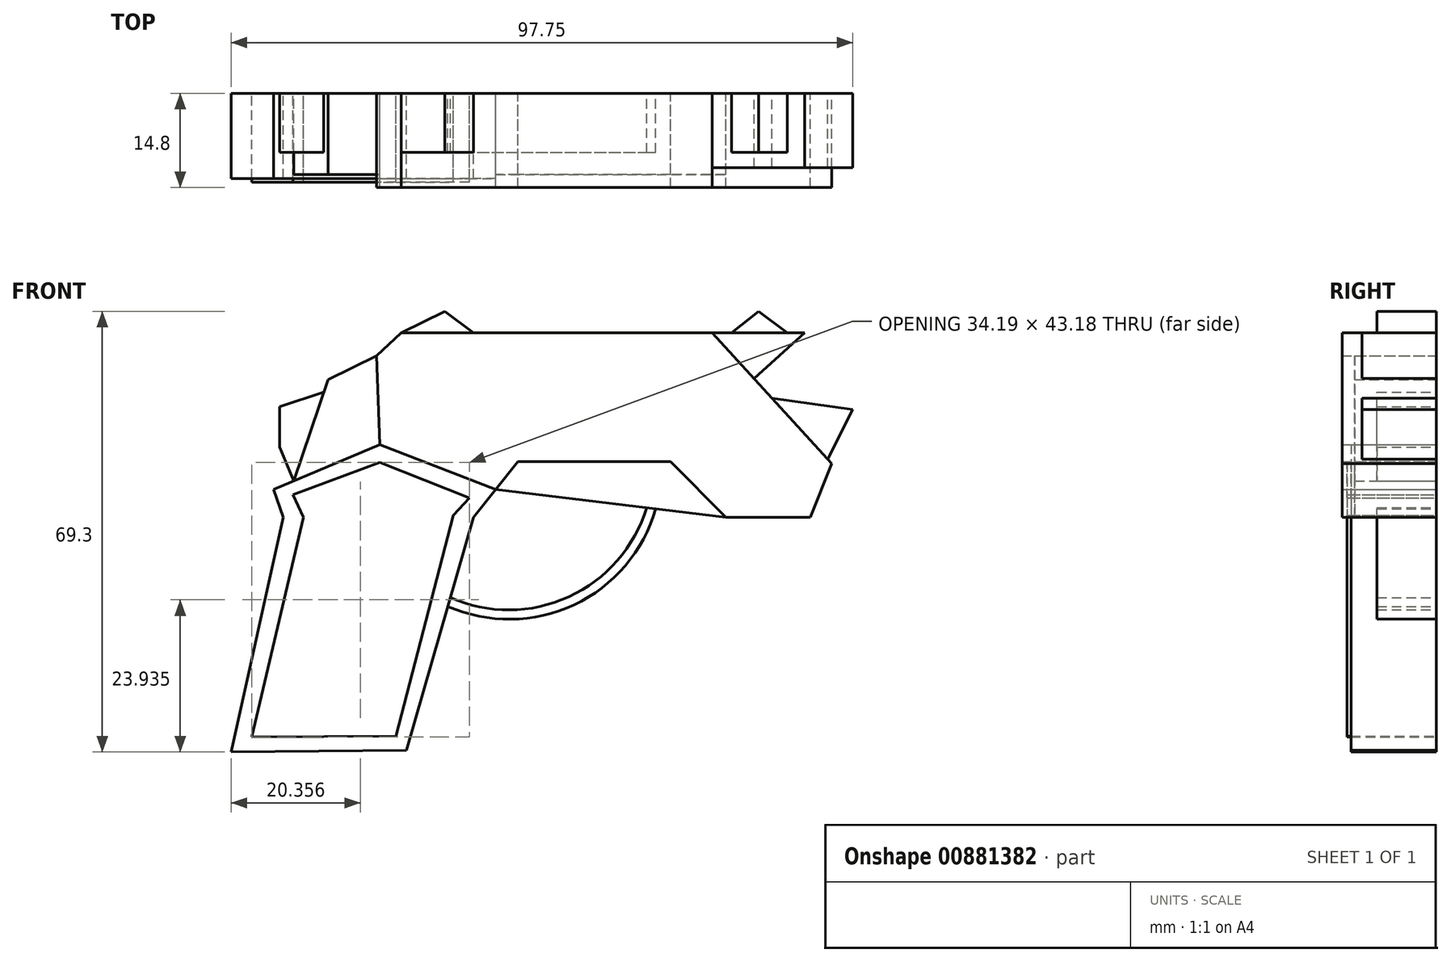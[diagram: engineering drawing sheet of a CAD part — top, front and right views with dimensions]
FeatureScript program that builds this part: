
annotation { "Feature Type Name" : "Feature", "Feature Type Description" : "" }
export const myFeature = defineFeature(function(context is Context, id is Id, definition is map)
    precondition{}
    {
        {
            var Q0;
            Q0=qCreatedBy(makeId("Front.planeOp"),FACE);
            var sketch = newSketch(context, id + "F0", { "sketchPlane" : qUnion([Q0])});
            skLineSegment(sketch, "E0", {"start": v(-19.98, -27.94) * mm, "end": v(-9.39, 8.68) * mm});
            skLineSegment(sketch, "E1", {"start": v(-9.39, 37.73) * mm, "end": v(-13.93, 41.06) * mm});
            skLineSegment(sketch, "E2", {"start": v(-39.34, 8.68) * mm, "end": v(-47.52, -28.24) * mm});
            skLineSegment(sketch, "E3", {"start": v(-47.52, -28.24) * mm, "end": v(-19.98, -27.94) * mm});
            skLineSegment(sketch, "E4", {"start": v(30.26, 8.68) * mm, "end": v(43.57, 8.68) * mm});
            skLineSegment(sketch, "E5", {"start": v(30.26, 8.68) * mm, "end": v(21.6, 17.45) * mm});
            skLineSegment(sketch, "E6", {"start": v(21.6, 17.45) * mm, "end": v(-2.43, 17.45) * mm});
            skLineSegment(sketch, "E7", {"start": v(46.9, 17.15) * mm, "end": v(28.14, 37.73) * mm});
            skLineSegment(sketch, "E8", {"start": v(-2.43, 17.45) * mm, "end": v(-9.39, 8.68) * mm});
            skLineSegment(sketch, "E9", {"start": v(42.66, 37.73) * mm, "end": v(28.14, 37.73) * mm});
            skLineSegment(sketch, "E10", {"start": v(50.23, 25.62) * mm, "end": v(37.52, 27.44) * mm});
            skLineSegment(sketch, "E11", {"start": v(-5.9, 13.06) * mm, "end": v(30.26, 8.68) * mm});
            skArc(sketch, "E12", {"start": v(-13.04, -3.94) * mm, "mid": v(5.57, -3.83) * mm, "end": v(17.81, 10.19) * mm});
            skLineSegment(sketch, "E13", {"start": v(-7.65, 10.87) * mm, "end": v(-12.14, -4.32) * mm});
            skLineSegment(sketch, "E14", {"start": v(0.63, 6.64) * mm, "end": v(-1.72, 0) * mm});
            skLineSegment(sketch, "E15", {"start": v(0, 7.28) * mm, "end": v(-2.68, 0) * mm});
            skLineSegment(sketch, "E16", {"start": v(-2.68, 0) * mm, "end": v(-0.76, -5.67) * mm});
            skLineSegment(sketch, "E17", {"start": v(0, 7.28) * mm, "end": v(5.01, 11.74) * mm});
            skLineSegment(sketch, "E18", {"start": v(0.63, 6.64) * mm, "end": v(2.5, 9.5) * mm});
            skLineSegment(sketch, "E19", {"start": v(-1.72, 0) * mm, "end": v(-1.72, -2.83) * mm});
            skArc(sketch, "E20", {"start": v(-13.44, -5.33) * mm, "mid": v(6.4, -5.08) * mm, "end": v(19.25, 10.01) * mm});
            skLineSegment(sketch, "E21", {"start": v(41.03, 36.24) * mm, "end": v(46.3, 36.24) * mm});
            skLineSegment(sketch, "E22", {"start": v(46.3, 36.24) * mm, "end": v(46.3, 26.7) * mm});
            skLineSegment(sketch, "E23", {"start": v(46.3, 26.7) * mm, "end": v(42.66, 26.7) * mm});
            skLineSegment(sketch, "E24", {"start": v(48.73, 34.52) * mm, "end": v(48.73, 28.62) * mm});
            skLineSegment(sketch, "E25", {"start": v(48.73, 28.62) * mm, "end": v(46.3, 26.7) * mm});
            skLineSegment(sketch, "E26", {"start": v(48.73, 34.52) * mm, "end": v(46.3, 36.24) * mm});
            skLineSegment(sketch, "E27", {"start": v(46.9, 17.15) * mm, "end": v(43.57, 8.68) * mm});
            skLineSegment(sketch, "E28", {"start": v(50.23, 25.62) * mm, "end": v(46.3, 17.8) * mm});
            skLineSegment(sketch, "E29", {"start": v(38.87, 28.5) * mm, "end": v(38.87, 27.25) * mm});
            skLineSegment(sketch, "E30", {"start": v(-24.14, 20.12) * mm, "end": v(-5.9, 13.06) * mm});
            skLineSegment(sketch, "E31", {"start": v(-24.14, 20.12) * mm, "end": v(-40.86, 13.06) * mm});
            skLineSegment(sketch, "E32", {"start": v(-9.39, 37.73) * mm, "end": v(28.14, 37.73) * mm});
            skLineSegment(sketch, "E33", {"start": v(-13.93, 41.06) * mm, "end": v(-20.75, 37.73) * mm});
            skLineSegment(sketch, "E34", {"start": v(-20.75, 37.73) * mm, "end": v(-9.39, 37.73) * mm});
            skLineSegment(sketch, "E35", {"start": v(-20.75, 37.73) * mm, "end": v(-24.67, 34.05) * mm});
            skLineSegment(sketch, "E36", {"start": v(-24.1, 17.29) * mm, "end": v(-37.78, 12.25) * mm});
            skLineSegment(sketch, "E37", {"start": v(-37.78, 12.25) * mm, "end": v(-36.16, 8.65) * mm});
            skLineSegment(sketch, "E38", {"start": v(-36.16, 8.65) * mm, "end": v(-44.26, -25.9) * mm});
            skLineSegment(sketch, "E39", {"start": v(-44.26, -25.9) * mm, "end": v(-21.59, -25.72) * mm});
            skLineSegment(sketch, "E40", {"start": v(-21.59, -25.72) * mm, "end": v(-12.59, 9) * mm});
            skLineSegment(sketch, "E41", {"start": v(-10.07, 11.7) * mm, "end": v(-12.59, 9) * mm});
            skLineSegment(sketch, "E42", {"start": v(-10.07, 11.7) * mm, "end": v(-24.1, 17.29) * mm});
            skLineSegment(sketch, "E43", {"start": v(-24.67, 34.05) * mm, "end": v(-24.14, 20.12) * mm});
            skLineSegment(sketch, "E44", {"start": v(-40.86, 13.06) * mm, "end": v(-39.34, 8.68) * mm});
            skLineSegment(sketch, "E45", {"start": v(-39.92, 19.75) * mm, "end": v(-37.66, 14.41) * mm});
            skLineSegment(sketch, "E46", {"start": v(-37.66, 14.41) * mm, "end": v(-32.3, 30.33) * mm});
            skLineSegment(sketch, "E47", {"start": v(-32.3, 30.33) * mm, "end": v(-24.67, 34.05) * mm});
            skLineSegment(sketch, "E48", {"start": v(-39.92, 19.75) * mm, "end": v(-39.92, 26.1) * mm});
            skLineSegment(sketch, "E49", {"start": v(-39.92, 26.1) * mm, "end": v(-32.97, 28.34) * mm});
            skLineSegment(sketch, "E50", {"start": v(31.16, 37.73) * mm, "end": v(35.4, 41.06) * mm});
            skPoint(sketch, "E50.endSnap0", {"position": v(35.4, 37.73) * mm});
            skLineSegment(sketch, "E51", {"start": v(35.4, 41.06) * mm, "end": v(39.94, 37.73) * mm});
            skLineSegment(sketch, "E52", {"start": v(48.73, 31.57) * mm, "end": v(36.9, 31.57) * mm});
            skLineSegment(sketch, "E53", {"start": v(36.9, 31.57) * mm, "end": v(35.91, 31.57) * mm});
            skLineSegment(sketch, "E54", {"start": v(35.91, 31.57) * mm, "end": v(48.73, 31.57) * mm});
            skLineSegment(sketch, "E55", {"start": v(41.03, 36.24) * mm, "end": v(35.91, 31.57) * mm});
            skLineSegment(sketch, "E56", {"start": v(35.91, 31.57) * mm, "end": v(34.73, 30.5) * mm});
            skLineSegment(sketch, "E57", {"start": v(42.66, 37.73) * mm, "end": v(41.03, 36.24) * mm});
            skLineSegment(sketch, "E58", {"start": v(35.91, 31.57) * mm, "end": v(38.87, 28.5) * mm});
            skSolve(sketch);
        }
        {
            var Q0;
            Q0=makeQuery(id+"F0.imprint","IMPRINT",FACE,{"disambiguationData":[TD([[makeQuery(id+"F0.imprint","IMPRINT",EDGE,{"derivedFrom":sQuery(id+"F0.wireOp",EDGE,"E4")}),1.0]])]});
            extrude(context, id + "F1", {"entities" : qUnion([Q0]), "depth" : 14.8 * mm, "offsetDistance" : 25 * mm});
        }
        {
            var Q0;
            {var subQ5=sQuery(id+"F0.wireOp",EDGE,"E43");Q0=makeQuery(id+"F0.imprint","IMPRINT",FACE,{"disambiguationData":[TD([[makeQuery(id+"F0.imprint","IMPRINT",EDGE,{"derivedFrom":subQ5}),-1.0]])]});}
            var Q1;
            {var subQ7=sQuery(id+"F0.wireOp",EDGE,"E5");Q1=makeQuery(id+"F0.imprint","IMPRINT",FACE,{"disambiguationData":[TD([[makeQuery(id+"F0.imprint","IMPRINT",EDGE,{"derivedFrom":subQ7}),1.0]])]});}
            extrude(context, id + "F2", {"entities" : qUnion([Q0, Q1]), "depth" : 12.8 * mm, "offsetDistance" : 25 * mm});
        }
        {
            var Q0;
            Q0=makeQuery(id+"F0.imprint","IMPRINT",FACE,{"disambiguationData":[TD([[makeQuery(id+"F0.imprint","IMPRINT",EDGE,{"derivedFrom":sQuery(id+"F0.wireOp",EDGE,"E36")}),1.0]])]});
            extrude(context, id + "F3", {"entities" : qUnion([Q0]), "depth" : 14 * mm, "offsetDistance" : 25 * mm});
        }
        {
            var Q0;
            Q0=makeQuery(id+"F0.imprint","IMPRINT",FACE,{"disambiguationData":[TD([[makeQuery(id+"F0.imprint","IMPRINT",EDGE,{"derivedFrom":sQuery(id+"F0.wireOp",EDGE,"E2")}),1.0]])]});
            extrude(context, id + "F4", {"entities" : qUnion([Q0]), "depth" : 13.4 * mm, "offsetDistance" : 25 * mm});
        }
        {
            var Q0;
            {var subQ0=sQuery(id+"F0.wireOp",EDGE,"E45");Q0=makeQuery(id+"F0.imprint","IMPRINT",FACE,{"disambiguationData":[TD([[makeQuery(id+"F0.imprint","IMPRINT",EDGE,{"derivedFrom":subQ0}),1.0]])]});}
            var Q1;
            Q1=makeQuery(id+"F0.imprint","IMPRINT",FACE,{"disambiguationData":[TD([[makeQuery(id+"F0.imprint","IMPRINT",EDGE,{"derivedFrom":sQuery(id+"F0.wireOp",EDGE,"E1")}),1.0]])]});
            var Q2;
            {var subQ0=sQuery(id+"F0.wireOp",EDGE,"E50");Q2=makeQuery(id+"F0.imprint","IMPRINT",FACE,{"disambiguationData":[TD([[makeQuery(id+"F0.imprint","IMPRINT",EDGE,{"derivedFrom":subQ0}),-1.0]])]});}
            var Q3;
            {var subQ3=sQuery(id+"F0.wireOp",EDGE,"E20");Q3=makeQuery(id+"F0.imprint","IMPRINT",FACE,{"disambiguationData":[TD([[makeQuery(id+"F0.imprint","IMPRINT",EDGE,{"derivedFrom":subQ3}),1.0]])]});}
            extrude(context, id + "F5", {"entities" : qUnion([Q0, Q1, Q2, Q3]), "depth" : 9.3 * mm, "offsetDistance" : 25 * mm});
        }
        {
            var Q0;
            Q0=makeQuery(id+"F0.imprint","IMPRINT",FACE,{"disambiguationData":[TD([[makeQuery(id+"F0.imprint","IMPRINT",EDGE,{"derivedFrom":sQuery(id+"F0.wireOp",EDGE,"E55")}),-1.0]])]});
            var Q1;
            {var subQ4=sQuery(id+"F0.wireOp",EDGE,"E28");Q1=makeQuery(id+"F0.imprint","IMPRINT",FACE,{"disambiguationData":[TD([[makeQuery(id+"F0.imprint","IMPRINT",EDGE,{"derivedFrom":subQ4}),-1.0]])]});}
            extrude(context, id + "F6", {"entities" : qUnion([Q0, Q1]), "depth" : 11.7 * mm, "offsetDistance" : 25 * mm});
        }
    });
